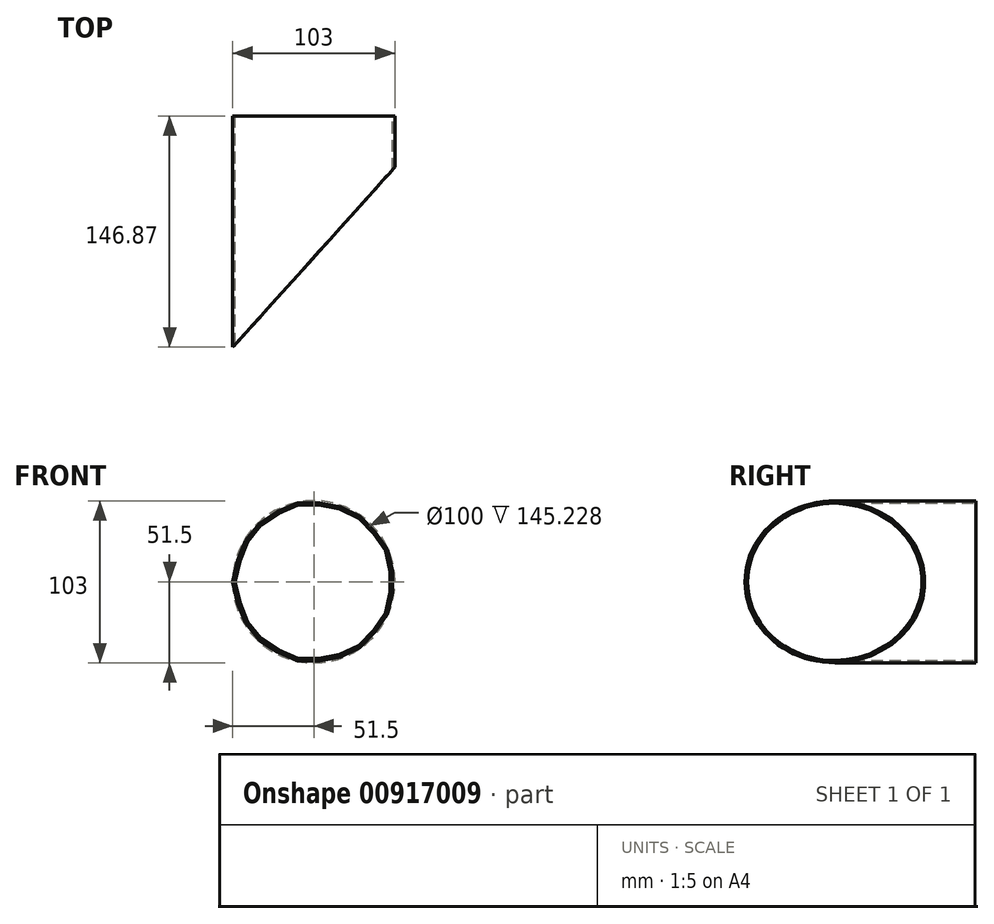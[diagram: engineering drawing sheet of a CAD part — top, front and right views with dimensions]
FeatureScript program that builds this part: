
annotation { "Feature Type Name" : "Feature", "Feature Type Description" : "" }
export const myFeature = defineFeature(function(context is Context, id is Id, definition is map)
    precondition{}
    {
        {
            var Q0;
            Q0=qCreatedBy(makeId("Front.planeOp"),FACE);
            var sketch = newSketch(context, id + "F0", { "sketchPlane" : qUnion([Q0])});
            skCircle(sketch, "E0", {"center": v(0, 0) * mm, "radius": 50 * mm});
            skCircle(sketch, "E1.0", {"center": v(0, 0) * mm, "radius": 51.5 * mm});
            skSolve(sketch);
        }
        {
            var Q0;
            Q0=makeQuery(id+"F0.imprint","IMPRINT",FACE,{"disambiguationData":[TD([[makeQuery(id+"F0.imprint","IMPRINT",EDGE,{"derivedFrom":sQuery(id+"F0.wireOp",EDGE,"E0")}),-1.0]])]});
            extrude(context, id + "F1", {"entities" : qUnion([Q0]), "depth" : 160 * mm, "offsetDistance" : 25 * mm});
        }
        {
            var Q0;
            Q0=qCreatedBy(makeId("Top.planeOp"),FACE);
            var sketch = newSketch(context, id + "F2", { "sketchPlane" : qUnion([Q0])});
            skLineSegment(sketch, "E2", {"start": v(0, 0) * mm, "end": v(44.59, -40.15) * mm});
            skLineSegment(sketch, "E3", {"start": v(0, 0) * mm, "end": v(127.55, 0) * mm, "construction": true});
            skSolve(sketch);
        }
        {
            var Q0;
            Q0=sQuery(id+"F2.wireOp",VERTEX,"E2.end");
            var Q1;
            Q1=sQuery(id+"F2.wireOp",EDGE,"E2");
            cPlane(context, id + "F3", {"entities" : qUnion([Q0, Q1]), "cplaneType" : CPlaneType.LINE_POINT, "offset" : 25 * mm, "width" : 150 * mm, "height" : 150 * mm});
        }
        {
            var Q0;
            Q0=makeQuery(id+"F1.opExtrude","CAP_FACE",FACE,{"disambiguationData":[OSD([sQuery(id+"F0.wireOp",EDGE,"E0"),sQuery(id+"F0.wireOp",EDGE,"E1.0")])],"isStart":false});
            var Q1;
            Q1=qCreatedBy(id+"F3.planeOp",FACE);
            extrude(context, id + "F4", {"entities" : qUnion([Q0]), "operationType" : NewBodyOperationType.REMOVE, "endBound" : BoundingType.UP_TO_SURFACE, "oppositeDirection" : true, "depth" : 25 * mm, "endBoundEntityFace" : qUnion([Q1]), "offsetDistance" : 25 * mm});
        }
    });
